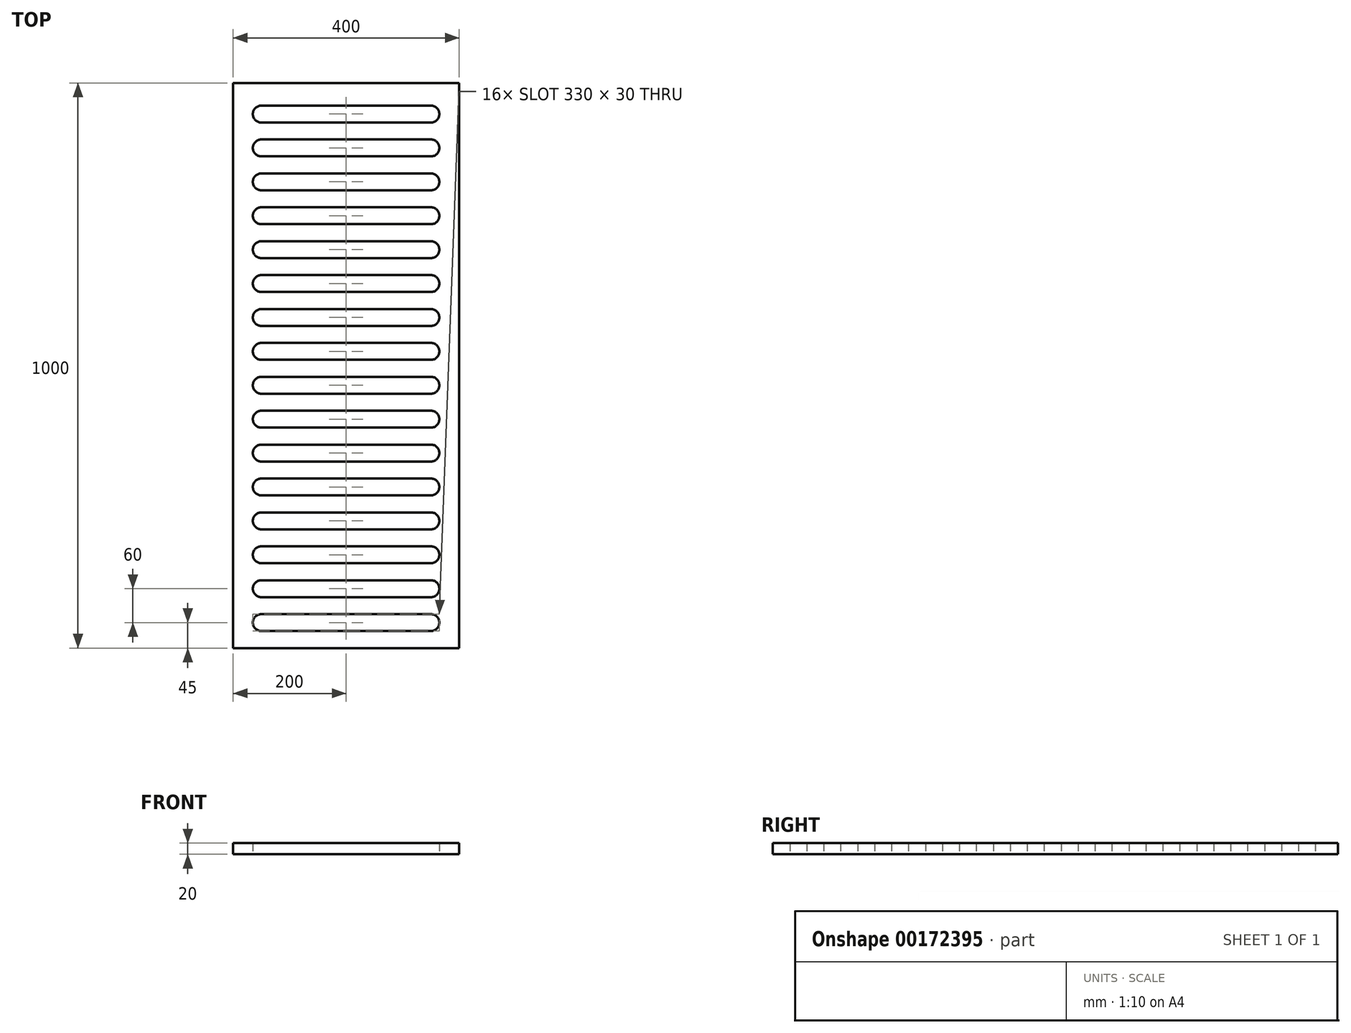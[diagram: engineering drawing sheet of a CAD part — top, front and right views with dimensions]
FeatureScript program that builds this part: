
annotation { "Feature Type Name" : "Feature", "Feature Type Description" : "" }
export const myFeature = defineFeature(function(context is Context, id is Id, definition is map)
    precondition{}
    {
        {
            var Q0;
            Q0=qCreatedBy(makeId("Top.planeOp"),FACE);
            var sketch = newSketch(context, id + "F0", { "sketchPlane" : qUnion([Q0])});
            skLineSegment(sketch, "E0.bottom", {"start": v(0, 0) * mm, "end": v(400, 0) * mm});
            skLineSegment(sketch, "E0.top", {"start": v(0, 1000) * mm, "end": v(400, 1000) * mm});
            skLineSegment(sketch, "E0.left", {"start": v(0, 0) * mm, "end": v(0, 1000) * mm});
            skLineSegment(sketch, "E0.right", {"start": v(400, 0) * mm, "end": v(400, 1000) * mm});
            skLineSegment(sketch, "E1", {"start": v(50, 30) * mm, "end": v(350, 30) * mm});
            skLineSegment(sketch, "E2", {"start": v(50, 60) * mm, "end": v(350, 60) * mm});
            skArc(sketch, "E3", {"start": v(50, 60) * mm, "mid": v(35, 45) * mm, "end": v(50, 30) * mm});
            skArc(sketch, "E4", {"start": v(350, 30) * mm, "mid": v(365, 45) * mm, "end": v(350, 60) * mm});
            skLineSegment(sketch, "E5.0.1.0", {"start": v(50, 90) * mm, "end": v(350, 90) * mm});
            skArc(sketch, "E5.0.1.1", {"start": v(350, 90) * mm, "mid": v(365, 105) * mm, "end": v(350, 120) * mm});
            skArc(sketch, "E5.0.1.2", {"start": v(50, 120) * mm, "mid": v(35, 105) * mm, "end": v(50, 90) * mm});
            skLineSegment(sketch, "E5.0.1.3", {"start": v(50, 120) * mm, "end": v(350, 120) * mm});
            skLineSegment(sketch, "E5.0.2.0", {"start": v(50, 150) * mm, "end": v(350, 150) * mm});
            skArc(sketch, "E5.0.2.1", {"start": v(350, 150) * mm, "mid": v(365, 165) * mm, "end": v(350, 180) * mm});
            skArc(sketch, "E5.0.2.2", {"start": v(50, 180) * mm, "mid": v(35, 165) * mm, "end": v(50, 150) * mm});
            skLineSegment(sketch, "E5.0.2.3", {"start": v(50, 180) * mm, "end": v(350, 180) * mm});
            skLineSegment(sketch, "E5.0.3.0", {"start": v(50, 210) * mm, "end": v(350, 210) * mm});
            skArc(sketch, "E5.0.3.1", {"start": v(350, 210) * mm, "mid": v(365, 225) * mm, "end": v(350, 240) * mm});
            skArc(sketch, "E5.0.3.2", {"start": v(50, 240) * mm, "mid": v(35, 225) * mm, "end": v(50, 210) * mm});
            skLineSegment(sketch, "E5.0.3.3", {"start": v(50, 240) * mm, "end": v(350, 240) * mm});
            skLineSegment(sketch, "E5.0.4.0", {"start": v(50, 270) * mm, "end": v(350, 270) * mm});
            skArc(sketch, "E5.0.4.1", {"start": v(350, 270) * mm, "mid": v(365, 285) * mm, "end": v(350, 300) * mm});
            skArc(sketch, "E5.0.4.2", {"start": v(50, 300) * mm, "mid": v(35, 285) * mm, "end": v(50, 270) * mm});
            skLineSegment(sketch, "E5.0.4.3", {"start": v(50, 300) * mm, "end": v(350, 300) * mm});
            skLineSegment(sketch, "E5.0.5.0", {"start": v(50, 330) * mm, "end": v(350, 330) * mm});
            skArc(sketch, "E5.0.5.1", {"start": v(350, 330) * mm, "mid": v(365, 345) * mm, "end": v(350, 360) * mm});
            skArc(sketch, "E5.0.5.2", {"start": v(50, 360) * mm, "mid": v(35, 345) * mm, "end": v(50, 330) * mm});
            skLineSegment(sketch, "E5.0.5.3", {"start": v(50, 360) * mm, "end": v(350, 360) * mm});
            skLineSegment(sketch, "E5.0.6.0", {"start": v(50, 390) * mm, "end": v(350, 390) * mm});
            skArc(sketch, "E5.0.6.1", {"start": v(350, 390) * mm, "mid": v(365, 405) * mm, "end": v(350, 420) * mm});
            skArc(sketch, "E5.0.6.2", {"start": v(50, 420) * mm, "mid": v(35, 405) * mm, "end": v(50, 390) * mm});
            skLineSegment(sketch, "E5.0.6.3", {"start": v(50, 420) * mm, "end": v(350, 420) * mm});
            skLineSegment(sketch, "E5.0.7.0", {"start": v(50, 450) * mm, "end": v(350, 450) * mm});
            skArc(sketch, "E5.0.7.1", {"start": v(350, 450) * mm, "mid": v(365, 465) * mm, "end": v(350, 480) * mm});
            skArc(sketch, "E5.0.7.2", {"start": v(50, 480) * mm, "mid": v(35, 465) * mm, "end": v(50, 450) * mm});
            skLineSegment(sketch, "E5.0.7.3", {"start": v(50, 480) * mm, "end": v(350, 480) * mm});
            skLineSegment(sketch, "E5.0.8.0", {"start": v(50, 510) * mm, "end": v(350, 510) * mm});
            skArc(sketch, "E5.0.8.1", {"start": v(350, 510) * mm, "mid": v(365, 525) * mm, "end": v(350, 540) * mm});
            skArc(sketch, "E5.0.8.2", {"start": v(50, 540) * mm, "mid": v(35, 525) * mm, "end": v(50, 510) * mm});
            skLineSegment(sketch, "E5.0.8.3", {"start": v(50, 540) * mm, "end": v(350, 540) * mm});
            skLineSegment(sketch, "E5.0.9.0", {"start": v(50, 570) * mm, "end": v(350, 570) * mm});
            skArc(sketch, "E5.0.9.1", {"start": v(350, 570) * mm, "mid": v(365, 585) * mm, "end": v(350, 600) * mm});
            skArc(sketch, "E5.0.9.2", {"start": v(50, 600) * mm, "mid": v(35, 585) * mm, "end": v(50, 570) * mm});
            skLineSegment(sketch, "E5.0.9.3", {"start": v(50, 600) * mm, "end": v(350, 600) * mm});
            skLineSegment(sketch, "E5.0.10.0", {"start": v(50, 630) * mm, "end": v(350, 630) * mm});
            skArc(sketch, "E5.0.10.1", {"start": v(350, 630) * mm, "mid": v(365, 645) * mm, "end": v(350, 660) * mm});
            skArc(sketch, "E5.0.10.2", {"start": v(50, 660) * mm, "mid": v(35, 645) * mm, "end": v(50, 630) * mm});
            skLineSegment(sketch, "E5.0.10.3", {"start": v(50, 660) * mm, "end": v(350, 660) * mm});
            skLineSegment(sketch, "E5.0.11.0", {"start": v(50, 690) * mm, "end": v(350, 690) * mm});
            skArc(sketch, "E5.0.11.1", {"start": v(350, 690) * mm, "mid": v(365, 705) * mm, "end": v(350, 720) * mm});
            skArc(sketch, "E5.0.11.2", {"start": v(50, 720) * mm, "mid": v(35, 705) * mm, "end": v(50, 690) * mm});
            skLineSegment(sketch, "E5.0.11.3", {"start": v(50, 720) * mm, "end": v(350, 720) * mm});
            skLineSegment(sketch, "E5.0.12.0", {"start": v(50, 750) * mm, "end": v(350, 750) * mm});
            skArc(sketch, "E5.0.12.1", {"start": v(350, 750) * mm, "mid": v(365, 765) * mm, "end": v(350, 780) * mm});
            skArc(sketch, "E5.0.12.2", {"start": v(50, 780) * mm, "mid": v(35, 765) * mm, "end": v(50, 750) * mm});
            skLineSegment(sketch, "E5.0.12.3", {"start": v(50, 780) * mm, "end": v(350, 780) * mm});
            skLineSegment(sketch, "E5.0.13.0", {"start": v(50, 810) * mm, "end": v(350, 810) * mm});
            skArc(sketch, "E5.0.13.1", {"start": v(350, 810) * mm, "mid": v(365, 825) * mm, "end": v(350, 840) * mm});
            skArc(sketch, "E5.0.13.2", {"start": v(50, 840) * mm, "mid": v(35, 825) * mm, "end": v(50, 810) * mm});
            skLineSegment(sketch, "E5.0.13.3", {"start": v(50, 840) * mm, "end": v(350, 840) * mm});
            skLineSegment(sketch, "E5.0.14.0", {"start": v(50, 870) * mm, "end": v(350, 870) * mm});
            skArc(sketch, "E5.0.14.1", {"start": v(350, 870) * mm, "mid": v(365, 885) * mm, "end": v(350, 900) * mm});
            skArc(sketch, "E5.0.14.2", {"start": v(50, 900) * mm, "mid": v(35, 885) * mm, "end": v(50, 870) * mm});
            skLineSegment(sketch, "E5.0.14.3", {"start": v(50, 900) * mm, "end": v(350, 900) * mm});
            skLineSegment(sketch, "E5.0.15.0", {"start": v(50, 930) * mm, "end": v(350, 930) * mm});
            skArc(sketch, "E5.0.15.1", {"start": v(350, 930) * mm, "mid": v(365, 945) * mm, "end": v(350, 960) * mm});
            skArc(sketch, "E5.0.15.2", {"start": v(50, 960) * mm, "mid": v(35, 945) * mm, "end": v(50, 930) * mm});
            skLineSegment(sketch, "E5.0.15.3", {"start": v(50, 960) * mm, "end": v(350, 960) * mm});
            skLineSegment(sketch, "E5.direction1", {"start": v(50, 30) * mm, "end": v(25, 30) * mm, "construction": true});
            skLineSegment(sketch, "E5.direction2", {"start": v(50, 30) * mm, "end": v(50, 90) * mm, "construction": true});
            skSolve(sketch);
        }
        {
            var Q0;
            Q0 = qSketchRegion(id + "F0", true);
            extrude(context, id + "F1", {"entities" : qUnion([Q0]), "depth" : 20 * mm});
        }
    });
